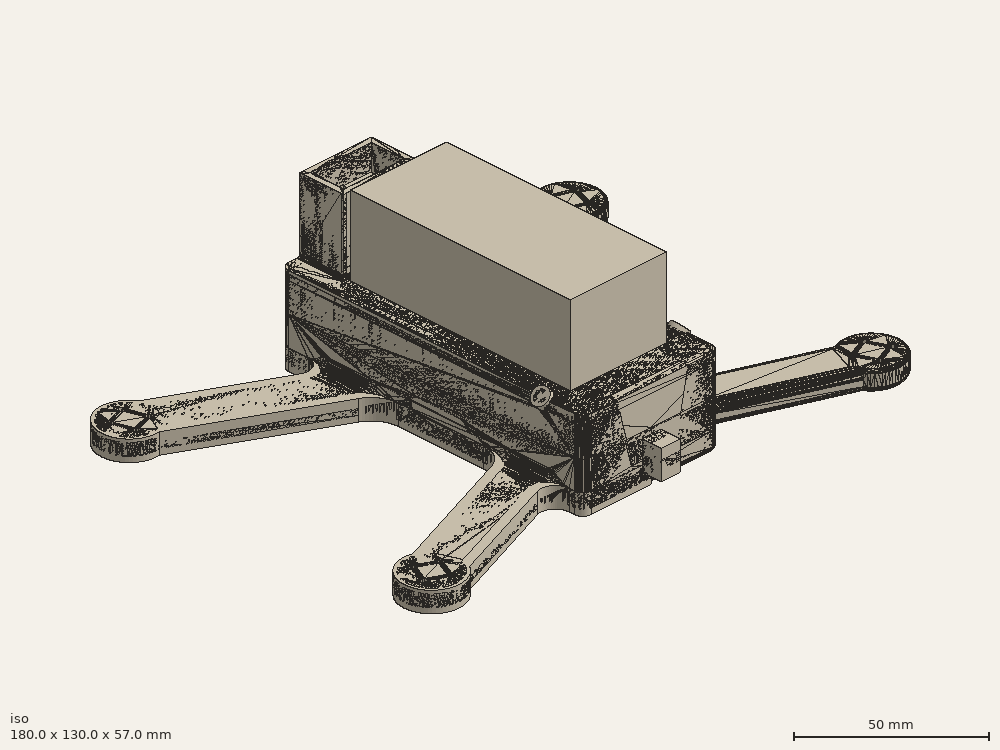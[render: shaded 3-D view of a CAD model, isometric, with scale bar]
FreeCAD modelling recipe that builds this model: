
FCSTD DOCUMENT  (FreeCAD 0.16R6700 (Git))
Label: fuselage3
License: All rights reserved
LicenseURL: http://en.wikipedia.org/wiki/All_rights_reserved
objects: Sketcher::SketchObject×24, PartDesign::Fillet×13, PartDesign::Pocket×12, PartDesign::Pad×11, Part::Fillet×4, Mesh::Feature×3, Part::Mirroring×2, Part::MultiFuse×2, Part::Revolution×1, Part::Cut×1, Part::Cylinder×1
note: 94 computed .brp shape members not serialized (recipe doc carries the construction recipe); baked Part::Feature solids carry a one-line shape summary decoded from their .brp

FEATURE [Mesh::Feature] cam_holder2
FEATURE [Sketcher::SketchObject] Sketch
  sketch-geometry (41):
    g0: LineSegment [constr] StartX=-80 StartY=55 StartZ=0 EndX=-80 EndY=-55 EndZ=0
    g1: LineSegment [constr] StartX=-80 StartY=55 StartZ=0 EndX=-25 EndY=55 EndZ=0
    g2: LineSegment [constr] StartX=-25 StartY=55 StartZ=0 EndX=25 EndY=55 EndZ=0
    g3: LineSegment [constr] StartX=25 StartY=55 StartZ=0 EndX=25 EndY=-55 EndZ=0
    g4: LineSegment [constr] StartX=25 StartY=-55 StartZ=0 EndX=-25 EndY=-55 EndZ=0
    g5: LineSegment [constr] StartX=-80 StartY=-55 StartZ=0 EndX=-25 EndY=-55 EndZ=0
    g6: ArcOfCircle CenterX=-80 CenterY=55 CenterZ=0 NormalX=0 NormalY=0 NormalZ=1 Radius=10 StartAngle=0.531084 EndAngle=4.82619
    g7: LineSegment StartX=-71.3774 StartY=60.0647 StartZ=0 EndX=-32.233 EndY=40.5263 EndZ=0
    g8: LineSegment StartX=-78.8644 StartY=45.0647 StartZ=0 EndX=-30.5341 EndY=20.9413 EndZ=0
    g9: LineSegment StartX=-25 StartY=11.9939 StartZ=0 EndX=-25 EndY=-18.7062 EndZ=0
    g10: ArcOfCircle CenterX=-80 CenterY=-55 CenterZ=0 NormalX=0 NormalY=0 NormalZ=1 Radius=10 StartAngle=1.29221 EndAngle=5.71447
    g11: LineSegment StartX=-77.2501 StartY=-45.3855 StartZ=0 EndX=-31.4609 EndY=-28.059 EndZ=0
    g12: LineSegment StartX=-71.5741 StartY=-60.3855 StartZ=0 EndX=-31.7695 EndY=-45.3236 EndZ=0
    g13: LineSegment StartX=0 StartY=55 StartZ=0 EndX=0 EndY=-55 EndZ=0
    g14: LineSegment [constr] StartX=-77.2501 StartY=-45.3855 StartZ=0 EndX=-71.5741 EndY=-60.3855 EndZ=0
    g15: LineSegment [constr] StartX=-71.3774 StartY=60.0647 StartZ=0 EndX=-78.8644 EndY=45.0647 EndZ=0
    g16: Circle CenterX=-77.5437 CenterY=59.9211 CenterZ=0 NormalX=0 NormalY=0 NormalZ=1 Radius=1.15
    g17: Circle CenterX=-84.9211 CenterY=57.4563 CenterZ=0 NormalX=0 NormalY=0 NormalZ=1 Radius=1.15
    g18: Circle CenterX=-82.4563 CenterY=50.0789 CenterZ=0 NormalX=0 NormalY=0 NormalZ=1 Radius=1.15
    g19: Circle CenterX=-75.0789 CenterY=52.5437 CenterZ=0 NormalX=0 NormalY=0 NormalZ=1 Radius=1.15
    g20: Circle [constr] CenterX=-80 CenterY=55 CenterZ=0 NormalX=0 NormalY=0 NormalZ=1 Radius=5.5
    g21: Circle CenterX=-81.9465 CenterY=-49.856 CenterZ=0 NormalX=0 NormalY=0 NormalZ=1 Radius=1.15
    g22: Circle CenterX=-85.144 CenterY=-56.9465 CenterZ=0 NormalX=0 NormalY=0 NormalZ=1 Radius=1.15
    g23: Circle CenterX=-78.0535 CenterY=-60.144 CenterZ=0 NormalX=0 NormalY=0 NormalZ=1 Radius=1.15
    g24: Circle CenterX=-74.856 CenterY=-53.0535 CenterZ=0 NormalX=0 NormalY=0 NormalZ=1 Radius=1.15
    g25: Circle [constr] CenterX=-80 CenterY=-55 CenterZ=0 NormalX=0 NormalY=0 NormalZ=1 Radius=5.5
    g26: ArcOfCircle CenterX=-35 CenterY=-18.7062 CenterZ=0 NormalX=0 NormalY=0 NormalZ=1 Radius=10 StartAngle=5.07413 EndAngle=6.28319
    g27: ArcOfCircle CenterX=-35 CenterY=11.9939 CenterZ=0 NormalX=0 NormalY=0 NormalZ=1 Radius=10 StartAngle=0 EndAngle=1.10784
    g28: LineSegment StartX=-25 StartY=45 StartZ=0 EndX=-25 EndY=52 EndZ=0
    g29: LineSegment StartX=-22 StartY=55 StartZ=0 EndX=0 EndY=55 EndZ=0
    g30: ArcOfCircle CenterX=-30 CenterY=45 CenterZ=0 NormalX=0 NormalY=0 NormalZ=1 Radius=5 StartAngle=4.24943 EndAngle=6.28319
    g31: LineSegment [constr] StartX=-25 StartY=45 StartZ=0 EndX=-25 EndY=11.9939 EndZ=0
    g32: LineSegment StartX=-25 StartY=-50 StartZ=0 EndX=-25 EndY=-52 EndZ=0
    g33: ArcOfCircle CenterX=-30 CenterY=-50 CenterZ=0 NormalX=0 NormalY=0 NormalZ=1 Radius=5 StartAngle=0 EndAngle=1.93254
    g34: LineSegment StartX=0 StartY=-55 StartZ=0 EndX=-22 EndY=-55 EndZ=0
    g35: ArcOfCircle CenterX=-22 CenterY=52 CenterZ=0 NormalX=0 NormalY=0 NormalZ=1 Radius=3 StartAngle=1.5708 EndAngle=3.14159
    g36: ArcOfCircle CenterX=-22 CenterY=-52 CenterZ=0 NormalX=0 NormalY=0 NormalZ=1 Radius=3 StartAngle=3.14159 EndAngle=4.71239
    g37: LineSegment [constr] StartX=-80 StartY=-55 StartZ=0 EndX=-74.4121 EndY=-52.8855 EndZ=0
    g38: LineSegment [constr] StartX=-80 StartY=-55 StartZ=0 EndX=-78.0535 EndY=-60.144 EndZ=0
    g39: LineSegment [constr] StartX=-77.5437 StartY=59.9211 StartZ=0 EndX=-82.4563 EndY=50.0789 EndZ=0
    g40: LineSegment [constr] StartX=-84.9211 StartY=57.4563 StartZ=0 EndX=-75.0789 EndY=52.5437 EndZ=0
  constraints (110):
    c: Vertical(g0)
    c: Distance(g0) = 110
    c: Coincident(g1,g0)
    c: Horizontal(g1)
    c: Distance(g1) = 55
    c: Coincident(g2,g3)
    c: Coincident(g3,g4)
    c: Horizontal(g2)
    c: Horizontal(g4)
    c: Vertical(g3)
    c: Coincident(g2,g1)
    c: Distance(g2) = 50
    c: Coincident(g5,g0)
    c: Horizontal(g5)
    c: Symmetric(g1,g2,g-2)
    c: Symmetric(g3,g2,g-1)
    c: Coincident(g0,g6)
    c: Radius(g6) = 10
    c: PointOnObject(g13,g-2)
    c: Equal(g6,g10) = 10
    c: Coincident(g7,g0)
    c: Coincident(g0,g10)
    c: Coincident(g6,g7)
    c: Coincident(g6,g8)
    c: Coincident(g10,g11)
    c: Coincident(g10,g12)
    c: DistanceY(g6,g6) = 15
    c: DistanceY(g10,g10) = 15
    c: Coincident(g14,g10)
    c: Coincident(g14,g10)
    c: Coincident(g15,g6)
    c: Coincident(g15,g6)
    c: Coincident(g20,g0)
    c: Radius(g20) = 5.5
    c: Radius(g16) = 1.15
    c: Equal(g16,g17)
    c: Equal(g17,g19)
    c: Equal(g19,g18)
    c: Equal(g20,g25) = 5.5
    c: Equal(g16,g21) = 1.15
    c: Equal(g21,g22)
    c: Equal(g22,g24)
    c: Equal(g24,g23)
    c: Coincident(g25,g0)
    c: Tangent(g11,g26) = -1.5708
    c: Tangent(g9,g26) = 1.5708
    c: Tangent(g9,g27) = 1.5708
    c: Tangent(g8,g27) = 1.5708
    c: Radius(g27) = 10
    c: Vertical(g9)
    c: Radius(g26) = 10
    c: Parallel(g7,g8)
    c: Perpendicular(g7,g15)
    c: PointOnObject(g29,g-2)
    c: Horizontal(g29)
    c: Coincident(g13,g29)
    c: Tangent(g28,g30) = -1.5708
    c: Tangent(g7,g30) = -1.5708
    c: Coincident(g31,g28)
    c: Coincident(g31,g9)
    c: Vertical(g31)
    c: Vertical(g28)
    c: Radius(g30) = 5
    c: Parallel(g11,g12)
    c: Perpendicular(g11,g14)
    c: Coincident(g4,g5)
    c: Vertical(g32)
    c: Tangent(g32,g33) = 1.5708
    c: Tangent(g12,g33) = 1.5708
    c: Radius(g33) = 5
    c: PointOnObject(g32,g31)
    c: Coincident(g34,g13)
    c: Horizontal(g34)
    c: Vertical(g13)
    c: Tangent(g29,g35) = 1.5708
    c: Tangent(g28,g35) = 1.5708
    c: Radius(g35) = 3
    c: PointOnObject(g29,g2)
    c: DistanceY(g28,g29) = 10
    c: PointOnObject(g1,g31)
    c: Tangent(g34,g36) = 1.5708
    c: Tangent(g32,g36) = -1.5708
    c: Radius(g36) = 3
    c: PointOnObject(g34,g4)
    c: PointOnObject(g4,g32)
    c: DistanceY(g4,g32) = 5
    c: Coincident(g37,g0)
    c: PointOnObject(g37,g14)
    c: Perpendicular(g37,g14)
    c: PointOnObject(g24,g37)
    c: PointOnObject(g24,g25)
    c: PointOnObject(g22,g37)
    c: PointOnObject(g22,g25)
    c: Coincident(g38,g0)
    c: PointOnObject(g38,g25)
    c: Parallel(g38,g14)
    c: Coincident(g23,g38)
    c: Symmetric(g21,g23,g37)
    c: PointOnObject(g39,g20)
    c: PointOnObject(g39,g20)
    c: PointOnObject(g40,g20)
    c: PointOnObject(g40,g20)
    c: PointOnObject(g0,g40)
    c: PointOnObject(g0,g39)
    c: Parallel(g39,g15)
    c: Perpendicular(g39,g40)
    c: Coincident(g17,g40)
    c: Coincident(g18,g39)
    c: Coincident(g19,g40)
    c: Coincident(g16,g39)
FEATURE [PartDesign::Pad] Pad
  Length = 7
  Length2 = 100
  Sketch = -> Sketch
  Type = 0
FEATURE [Sketcher::SketchObject] Sketch001
  Placement = pos=(0,0,7) rot=(0,0,1;0rad)
  Support = -> Pad [Face28]
  sketch-geometry (6):
    g0: LineSegment StartX=0 StartY=52 StartZ=0 EndX=-21 EndY=52 EndZ=0
    g1: LineSegment StartX=-22 StartY=51 StartZ=0 EndX=-22 EndY=-51 EndZ=0
    g2: LineSegment StartX=-21 StartY=-52 StartZ=0 EndX=0 EndY=-52 EndZ=0
    g3: LineSegment StartX=0 StartY=-52 StartZ=0 EndX=0 EndY=52 EndZ=0
    g4: ArcOfCircle CenterX=-21 CenterY=-51 CenterZ=0 NormalX=0 NormalY=0 NormalZ=1 Radius=1 StartAngle=3.14159 EndAngle=4.71239
    g5: ArcOfCircle CenterX=-21 CenterY=51 CenterZ=0 NormalX=0 NormalY=0 NormalZ=1 Radius=1 StartAngle=1.5708 EndAngle=3.14159
  constraints (16):
    c: Coincident(g2,g3)
    c: Coincident(g3,g0)
    c: Horizontal(g0)
    c: Horizontal(g2)
    c: Vertical(g1)
    c: Vertical(g3)
    c: PointOnObject(g0,g-2)
    c: Symmetric(g0,g2,g-1)
    c: Tangent(g2,g4) = -1.5708
    c: Tangent(g1,g4) = -1.5708
    c: Radius(g4) = 1
    c: Tangent(g0,g5) = -1.5708
    c: Tangent(g1,g5) = -1.5708
    c: Radius(g5) = 1
    c: DistanceX(g1,g0) = 22
    c: Distance(g3) = 104
FEATURE [PartDesign::Pocket] Pocket
  Length = 2
  Sketch = -> Sketch001
  Type = 0
FEATURE [Sketcher::SketchObject] Sketch002
  Placement = pos=(0,0,7) rot=(0,0,1;0rad)
  Support = -> Pocket [Face5]
  sketch-geometry (12):
    g0: LineSegment StartX=0 StartY=52 StartZ=0 EndX=-21 EndY=52 EndZ=0
    g1: LineSegment StartX=-22 StartY=51 StartZ=0 EndX=-22 EndY=-51 EndZ=0
    g2: LineSegment StartX=-21 StartY=-52 StartZ=0 EndX=0 EndY=-52 EndZ=0
    g3: ArcOfCircle CenterX=-21 CenterY=-51 CenterZ=0 NormalX=0 NormalY=0 NormalZ=1 Radius=1 StartAngle=3.14159 EndAngle=4.71239
    g4: ArcOfCircle CenterX=-21 CenterY=51 CenterZ=0 NormalX=0 NormalY=0 NormalZ=1 Radius=1 StartAngle=1.5708 EndAngle=3.14159
    g5: LineSegment StartX=0 StartY=-52 StartZ=0 EndX=0 EndY=-55 EndZ=0
    g6: LineSegment StartX=0 StartY=-55 StartZ=0 EndX=-22 EndY=-55 EndZ=0
    g7: LineSegment StartX=-25 StartY=-52 StartZ=0 EndX=-25 EndY=52 EndZ=0
    g8: LineSegment StartX=-22 StartY=55 StartZ=0 EndX=0 EndY=55 EndZ=0
    g9: LineSegment StartX=0 StartY=55 StartZ=0 EndX=0 EndY=52 EndZ=0
    g10: ArcOfCircle CenterX=-22 CenterY=-52 CenterZ=0 NormalX=0 NormalY=0 NormalZ=1 Radius=3 StartAngle=3.14159 EndAngle=4.71239
    g11: ArcOfCircle CenterX=-22 CenterY=52 CenterZ=0 NormalX=0 NormalY=0 NormalZ=1 Radius=3 StartAngle=1.5708 EndAngle=3.14159
  constraints (31):
    c: Horizontal(g0)
    c: Horizontal(g2)
    c: Vertical(g1)
    c: PointOnObject(g0,g-2)
    c: Symmetric(g0,g2,g-1)
    c: Tangent(g2,g3) = -1.5708
    c: Tangent(g1,g3) = -1.5708
    c: Radius(g3) = 1
    c: Tangent(g0,g4) = -1.5708
    c: Tangent(g1,g4) = -1.5708
    c: Radius(g4) = 1
    c: DistanceX(g1,g0) = 22
    c: Coincident(g5,g2)
    c: Vertical(g5)
    c: Coincident(g5,g6)
    c: Horizontal(g6)
    c: Vertical(g7)
    c: Horizontal(g8)
    c: Coincident(g8,g9)
    c: Coincident(g9,g0)
    c: Vertical(g9)
    c: Tangent(g6,g10) = 1.5708
    c: Tangent(g7,g10) = 1.5708
    c: Radius(g10) = 3
    c: Tangent(g8,g11) = 1.5708
    c: Tangent(g7,g11) = 1.5708
    c: Radius(g11) = 3
    c: DistanceY(g5,g8) = 110
    c: DistanceX(g7,g1) = 3
    c: DistanceY(g0,g8) = 3
    c: DistanceY(g6,g2) = 3
FEATURE [PartDesign::Pad] Pad001  label="height here"
  Length = 10
  Length2 = 100
  Sketch = -> Sketch002
  Type = 0
FEATURE [Part::Fillet] Fillet
  Base = -> Pad001
  Edges = 9 edges r=3: [Edge10,Edge34,Edge35,Edge42,Edge45,Edge48,Edge56,Edge57,Edge86]
FEATURE [Part::Fillet] Fillet001
  Base = -> Fillet
  Edges = 17 edges r=2: [Edge3,Edge6,Edge14,Edge15,Edge16,Edge17,Edge18,Edge19,Edge20,Edge21,Edge22,Edge23,Edge24,Edge26,Edge27,Edge28,Edge29]
FEATURE [Part::Fillet] Fillet002  label="body half"
  Base = -> Fillet001
  Edges = 2 edges r=1: [Edge10,Edge159]
FEATURE [Sketcher::SketchObject] Sketch003
  ExternalGeometry = -> [Fillet002]
  Placement = pos=(0,0,0) rot=(1,0,0;3.14159rad)
  Support = -> Fillet002 [Face14]
  sketch-geometry (8):
    g0: Circle CenterX=-78.0535 CenterY=60.144 CenterZ=0 NormalX=0 NormalY=0 NormalZ=1 Radius=2.5
    g1: Circle CenterX=-85.144 CenterY=56.9465 CenterZ=0 NormalX=0 NormalY=0 NormalZ=1 Radius=2.5
    g2: Circle CenterX=-74.856 CenterY=53.0535 CenterZ=0 NormalX=0 NormalY=0 NormalZ=1 Radius=2.5
    g3: Circle CenterX=-81.9465 CenterY=49.856 CenterZ=0 NormalX=0 NormalY=0 NormalZ=1 Radius=2.5
    g4: Circle CenterX=-75.0789 CenterY=-52.5437 CenterZ=0 NormalX=0 NormalY=0 NormalZ=1 Radius=2.5
    g5: Circle CenterX=-82.4563 CenterY=-50.0789 CenterZ=0 NormalX=0 NormalY=0 NormalZ=1 Radius=2.5
    g6: Circle CenterX=-84.9211 CenterY=-57.4563 CenterZ=0 NormalX=0 NormalY=0 NormalZ=1 Radius=2.5
    g7: Circle CenterX=-77.5437 CenterY=-59.9211 CenterZ=0 NormalX=0 NormalY=0 NormalZ=1 Radius=2.5
  constraints (16):
    c: Coincident(g0,g-5)
    c: Radius(g0) = 2.5
    c: Equal(g0,g1) = 2.5
    c: Coincident(g1,g-4)
    c: Coincident(g2,g-6)
    c: Equal(g0,g3) = 2.5
    c: Coincident(g3,g-3)
    c: Equal(g2,g0)
    c: Coincident(g4,g-7)
    c: Coincident(g5,g-8)
    c: Coincident(g6,g-9)
    c: Coincident(g7,g-10)
    c: Equal(g6,g7)
    c: Equal(g7,g5)
    c: Equal(g5,g4)
    c: Equal(g4,g0)
FEATURE [PartDesign::Pocket] Pocket001
  Length = 5
  Sketch = -> Sketch003
  Type = 0
FEATURE [Part::Mirroring] Part__Mirroring  label="Pocket001 (Mirror #1)"
  Base = (0,0,0)
  Normal = (1,0,0)
  Source = -> Pocket001
FEATURE [Part::MultiFuse] Fusion  label="body"
  Shapes = -> [Part__Mirroring,Pocket001]
FEATURE [Sketcher::SketchObject] Sketch009
  Placement = pos=(-15,43,6) rot=(-1,0,0;1.5708rad)
  sketch-geometry (8):
    g0: LineSegment StartX=0 StartY=0 StartZ=0 EndX=20 EndY=0 EndZ=0
    g1: LineSegment StartX=20 StartY=0 StartZ=0 EndX=20 EndY=-26 EndZ=0
    g2: LineSegment StartX=10 StartY=-26 StartZ=0 EndX=0 EndY=-26 EndZ=0
    g3: LineSegment StartX=0 StartY=-26 StartZ=0 EndX=0 EndY=0 EndZ=0
    g4: LineSegment StartX=20 StartY=-26 StartZ=0 EndX=20 EndY=-41 EndZ=0
    g5: LineSegment StartX=20 StartY=-41 StartZ=0 EndX=10 EndY=-41 EndZ=0
    g6: LineSegment StartX=10 StartY=-41 StartZ=0 EndX=10 EndY=-26 EndZ=0
    g7: LineSegment [constr] StartX=10 StartY=-26 StartZ=0 EndX=20 EndY=-26 EndZ=0
  constraints (22):
    c: Coincident(g0,g1)
    c: Coincident(g2,g3)
    c: Coincident(g3,g0)
    c: Horizontal(g0)
    c: Horizontal(g2)
    c: Vertical(g1)
    c: Vertical(g3)
    c: Distance(g0) = 20
    c: DistanceY(g1,g1) = 26
    c: Coincident(g4,g1)
    c: Vertical(g4)
    c: DistanceY(g4,g4) = 15
    c: Coincident(g5,g4)
    c: Horizontal(g5)
    c: Distance(g5) = 10
    c: Coincident(g6,g5)
    c: Vertical(g6)
    c: Coincident(g2,g6)
    c: Coincident(g7,g2)
    c: Coincident(g7,g1)
    c: Horizontal(g7)
    c: Coincident(g0,g-1)
FEATURE [PartDesign::Pad] Pad003  label="video_tx_base"
  Length = 6
  Length2 = 100
  Placement = pos=(-15,43,6) rot=(-1,0,0;1.5708rad)
  Sketch = -> Sketch009
  Type = 0
FEATURE [Sketcher::SketchObject] Sketch010
  ExternalGeometry = -> [Pad003]
  Placement = pos=(-15,49,6) rot=(-1,0,0;1.5708rad)
  Support = -> Pad003 [Face9]
  sketch-geometry (8):
    g0: LineSegment StartX=0.5 StartY=-3 StartZ=0 EndX=19.5 EndY=-3 EndZ=0
    g1: LineSegment StartX=19.5 StartY=-3 StartZ=0 EndX=19.5 EndY=-23 EndZ=0
    g2: LineSegment StartX=19.5 StartY=-23 StartZ=0 EndX=0.5 EndY=-23 EndZ=0
    g3: LineSegment StartX=0.5 StartY=-23 StartZ=0 EndX=0.5 EndY=-3 EndZ=0
    g4: LineSegment StartX=10 StartY=-26 StartZ=0 EndX=20 EndY=-26 EndZ=0
    g5: LineSegment StartX=20 StartY=-26 StartZ=0 EndX=20 EndY=-41 EndZ=0
    g6: LineSegment StartX=20 StartY=-41 StartZ=0 EndX=10 EndY=-41 EndZ=0
    g7: LineSegment StartX=10 StartY=-26 StartZ=0 EndX=10 EndY=-41 EndZ=0
  constraints (21):
    c: Coincident(g0,g1)
    c: Coincident(g1,g2)
    c: Coincident(g2,g3)
    c: Coincident(g3,g0)
    c: Horizontal(g0)
    c: Horizontal(g2)
    c: Vertical(g1)
    c: Vertical(g3)
    c: Coincident(g4,g5)
    c: Coincident(g5,g6)
    c: Horizontal(g4)
    c: Horizontal(g6)
    c: Vertical(g5)
    c: Coincident(g4,g-3)
    c: Coincident(g5,g-4)
    c: Distance(g2) = 19
    c: Distance(g1) = 20
    c: DistanceX(g-1,g0) = 0.5
    c: DistanceY(g0,g-1) = 3
    c: Coincident(g7,g4)
    c: Coincident(g7,g6)
FEATURE [PartDesign::Pad] Pad004  label="video_tx"
  Length = 3
  Length2 = 100
  Placement = pos=(-15,43,6) rot=(-1,0,0;1.5708rad)
  Sketch = -> Sketch010
  Type = 0
FEATURE [Part::Fillet] Fillet003
  Base = -> Fusion
  Edges = 10 edges r=1: [Edge272,Edge274,Edge276,Edge278,Edge279,Edge367,Edge369,Edge371,Edge372,Edge373]
FEATURE [Sketcher::SketchObject] Sketch011
  Placement = pos=(0,0,17) rot=(0,0,1;0rad)
  Support = -> Fillet003 [Face2]
  sketch-geometry (16):
    g0: LineSegment StartX=-22 StartY=55 StartZ=0 EndX=22 EndY=55 EndZ=0
    g1: LineSegment StartX=25 StartY=52 StartZ=0 EndX=25 EndY=-52 EndZ=0
    g2: LineSegment StartX=22 StartY=-55 StartZ=0 EndX=-22 EndY=-55 EndZ=0
    g3: LineSegment StartX=-25 StartY=-52 StartZ=0 EndX=-25 EndY=52 EndZ=0
    g4: LineSegment StartX=-22 StartY=53.5 StartZ=0 EndX=22 EndY=53.5 EndZ=0
    g5: LineSegment StartX=23.5 StartY=52 StartZ=0 EndX=23.5 EndY=-52 EndZ=0
    g6: LineSegment StartX=22 StartY=-53.5 StartZ=0 EndX=-22 EndY=-53.5 EndZ=0
    g7: LineSegment StartX=-23.5 StartY=-52 StartZ=0 EndX=-23.5 EndY=52 EndZ=0
    g8: ArcOfCircle CenterX=-22 CenterY=-52 CenterZ=0 NormalX=0 NormalY=0 NormalZ=1 Radius=1.5 StartAngle=3.14159 EndAngle=4.71239
    g9: ArcOfCircle CenterX=-22 CenterY=52 CenterZ=0 NormalX=0 NormalY=0 NormalZ=1 Radius=1.5 StartAngle=1.5708 EndAngle=3.14159
    g10: ArcOfCircle CenterX=22 CenterY=52 CenterZ=0 NormalX=0 NormalY=0 NormalZ=1 Radius=1.5 StartAngle=0 EndAngle=1.5708
    g11: ArcOfCircle CenterX=22 CenterY=-52 CenterZ=0 NormalX=0 NormalY=0 NormalZ=1 Radius=1.5 StartAngle=4.71239 EndAngle=6.28319
    g12: ArcOfCircle CenterX=22 CenterY=-52 CenterZ=0 NormalX=0 NormalY=0 NormalZ=1 Radius=3 StartAngle=4.71239 EndAngle=6.28319
    g13: ArcOfCircle CenterX=-22 CenterY=-52 CenterZ=0 NormalX=0 NormalY=0 NormalZ=1 Radius=3 StartAngle=3.14159 EndAngle=4.71239
    g14: ArcOfCircle CenterX=-22 CenterY=52 CenterZ=0 NormalX=0 NormalY=0 NormalZ=1 Radius=3 StartAngle=1.5708 EndAngle=3.14159
    g15: ArcOfCircle CenterX=22 CenterY=52 CenterZ=0 NormalX=0 NormalY=0 NormalZ=1 Radius=3 StartAngle=0 EndAngle=1.5708
  constraints (39):
    c: Horizontal(g0)
    c: Horizontal(g2)
    c: Vertical(g1)
    c: Vertical(g3)
    c: Horizontal(g4)
    c: Horizontal(g6)
    c: Vertical(g5)
    c: Vertical(g7)
    c: Tangent(g6,g8) = 1.5708
    c: Tangent(g7,g8) = 1.5708
    c: Tangent(g7,g9) = 1.5708
    c: Tangent(g4,g9) = 1.5708
    c: Tangent(g4,g10) = 1.5708
    c: Tangent(g5,g10) = 1.5708
    c: Tangent(g5,g11) = 1.5708
    c: Tangent(g6,g11) = 1.5708
    c: Tangent(g1,g12) = 1.5708
    c: Tangent(g2,g12) = 1.5708
    c: Tangent(g2,g13) = 1.5708
    c: Tangent(g3,g13) = 1.5708
    c: Tangent(g3,g14) = 1.5708
    c: Tangent(g0,g14) = 1.5708
    c: Tangent(g0,g15) = 1.5708
    c: Tangent(g1,g15) = 1.5708
    c: Radius(g15) = 3
    c: Equal(g15,g14)
    c: Equal(g15,g13)
    c: Equal(g15,g12)
    c: Radius(g8) = 1.5
    c: Equal(g8,g11)
    c: Equal(g8,g10)
    c: Equal(g8,g9)
    c: DistanceY(g2,g0) = 110
    c: DistanceX(g3,g1) = 50
    c: Symmetric(g0,g0,g-2)
    c: Symmetric(g3,g3,g-1)
    c: Symmetric(g7,g7,g-1)
    c: Symmetric(g4,g4,g-2)
    c: Coincident(g8,g13)
FEATURE [PartDesign::Pad] Pad005
  Length = 10
  Length2 = 100
  Sketch = -> Sketch011
  Type = 0
FEATURE [PartDesign::Fillet] Fillet004
  Base = -> Pad005 [Edge489,Edge542,Edge491,Edge497,Edge493,Edge495,Edge479,Edge481,Edge487,Edge483,Edge485]
  Radius = 1
FEATURE [Mesh::Feature] cc3d_model  label="cc3d-model"
  Placement = pos=(0,0,15) rot=(0,0,-1;1.5708rad)
FEATURE [Sketcher::SketchObject] Sketch012
  Placement = pos=(25,0,0) rot=(0.57735,0.57735,0.57735;2.0944rad)
  Support = -> Fillet004 [Face67]
  sketch-geometry (4):
    g0: ArcOfCircle CenterX=-5 CenterY=13 CenterZ=0 NormalX=0 NormalY=0 NormalZ=1 Radius=5 StartAngle=1.5708 EndAngle=4.71239
    g1: ArcOfCircle CenterX=5 CenterY=13 CenterZ=0 NormalX=0 NormalY=0 NormalZ=1 Radius=5 StartAngle=4.71239 EndAngle=7.85398
    g2: LineSegment StartX=-5 StartY=8 StartZ=0 EndX=5 EndY=8 EndZ=0
    g3: LineSegment StartX=-5 StartY=18 StartZ=0 EndX=5 EndY=18 EndZ=0
  constraints (10):
    c: Tangent(g0,g3) = 1.5708
    c: Tangent(g0,g2) = -1.5708
    c: Tangent(g2,g1) = -1.5708
    c: Tangent(g3,g1) = 1.5708
    c: Horizontal(g2)
    c: Equal(g0,g1)
    c: DistanceY(g0,g0) = 10
    c: Distance(g3) = 10
    c: DistanceY(g-1,g1) = 13
    c: DistanceX(g0,g-1) = 5
FEATURE [PartDesign::Pocket] Pocket002
  Length = 5
  Sketch = -> Sketch012
  Type = 0
FEATURE [Sketcher::SketchObject] Sketch013
  Placement = pos=(0,0,5) rot=(0,0,1;0rad)
  Support = -> Pocket002 [Face14]
  sketch-geometry (8):
    g0: Circle CenterX=-15.25 CenterY=15.25 CenterZ=0 NormalX=0 NormalY=0 NormalZ=1 Radius=1.7
    g1: LineSegment [constr] StartX=-15.25 StartY=15.25 StartZ=0 EndX=15.25 EndY=15.25 EndZ=0
    g2: LineSegment [constr] StartX=15.25 StartY=15.25 StartZ=0 EndX=15.25 EndY=-15.25 EndZ=0
    g3: LineSegment [constr] StartX=15.25 StartY=-15.25 StartZ=0 EndX=-15.25 EndY=-15.25 EndZ=0
    g4: LineSegment [constr] StartX=-15.25 StartY=-15.25 StartZ=0 EndX=-15.25 EndY=15.25 EndZ=0
    g5: Circle CenterX=15.25 CenterY=15.25 CenterZ=0 NormalX=0 NormalY=0 NormalZ=1 Radius=1.7
    g6: Circle CenterX=15.25 CenterY=-15.25 CenterZ=0 NormalX=0 NormalY=0 NormalZ=1 Radius=1.7
    g7: Circle CenterX=-15.25 CenterY=-15.25 CenterZ=0 NormalX=0 NormalY=0 NormalZ=1 Radius=1.7
  constraints (22):
    c: Radius(g0) = 1.7
    c: Coincident(g1,g2)
    c: Coincident(g2,g3)
    c: Coincident(g3,g4)
    c: Coincident(g4,g1)
    c: Horizontal(g1)
    c: Horizontal(g3)
    c: Vertical(g2)
    c: Vertical(g4)
    c: Coincident(g1,g0)
    c: Distance(g1) = 30.5
    c: Distance(g4) = 30.5
    c: Symmetric(g3,g2,g-2)
    c: Symmetric(g1,g2,g-1)
    c: Equal(g0,g5) = 1.7
    c: Coincident(g1,g1)
    c: Coincident(g6,g2)
    c: Equal(g0,g7) = 1.7
    c: Coincident(g1,g3)
    c: Equal(g7,g6)
    c: Coincident(g3,g7)
    c: Coincident(g1,g5)
FEATURE [PartDesign::Pocket] Pocket003
  Length = 5
  Sketch = -> Sketch013
  Type = 0
FEATURE [Sketcher::SketchObject] Sketch014
  ExternalGeometry = -> [Pocket003]
  Placement = pos=(0,0,0) rot=(1,0,0;3.14159rad)
  Support = -> Pocket003 [Face37]
  sketch-geometry (4):
    g0: Circle CenterX=-15.25 CenterY=15.25 CenterZ=0 NormalX=0 NormalY=0 NormalZ=1 Radius=5
    g1: Circle CenterX=15.25 CenterY=15.25 CenterZ=0 NormalX=0 NormalY=0 NormalZ=1 Radius=5
    g2: Circle CenterX=15.25 CenterY=-15.25 CenterZ=0 NormalX=0 NormalY=0 NormalZ=1 Radius=5
    g3: Circle CenterX=-15.25 CenterY=-15.25 CenterZ=0 NormalX=0 NormalY=0 NormalZ=1 Radius=5
  constraints (8):
    c: Coincident(g0,g-3)
    c: Radius(g0) = 5
    c: Equal(g0,g1) = 5
    c: Coincident(g1,g-4)
    c: Coincident(g2,g-5)
    c: Coincident(g3,g-6)
    c: Equal(g0,g3)
    c: Equal(g3,g2)
FEATURE [PartDesign::Pocket] Pocket004
  Length = 2
  Sketch = -> Sketch014
  Type = 0
FEATURE [PartDesign::Fillet] Fillet005
  Base = -> Pocket004 [Edge172,Edge155,Edge157,Edge170]
  Radius = 1
FEATURE [Sketcher::SketchObject] Sketch015
  Placement = pos=(0,0,27) rot=(0,0,1;0rad)
  Support = -> Fillet005 [Face223]
  sketch-geometry (8):
    g0: LineSegment StartX=-22 StartY=55 StartZ=0 EndX=22 EndY=55 EndZ=0
    g1: LineSegment StartX=25 StartY=52 StartZ=0 EndX=25 EndY=-52 EndZ=0
    g2: LineSegment StartX=22 StartY=-55 StartZ=0 EndX=-22 EndY=-55 EndZ=0
    g3: LineSegment StartX=-25 StartY=-52 StartZ=0 EndX=-25 EndY=52 EndZ=0
    g4: ArcOfCircle CenterX=-22 CenterY=52 CenterZ=0 NormalX=0 NormalY=0 NormalZ=1 Radius=3 StartAngle=1.5708 EndAngle=3.14159
    g5: ArcOfCircle CenterX=22 CenterY=52 CenterZ=0 NormalX=0 NormalY=0 NormalZ=1 Radius=3 StartAngle=0 EndAngle=1.5708
    g6: ArcOfCircle CenterX=22 CenterY=-52 CenterZ=0 NormalX=0 NormalY=0 NormalZ=1 Radius=3 StartAngle=4.71239 EndAngle=6.28319
    g7: ArcOfCircle CenterX=-22 CenterY=-52 CenterZ=0 NormalX=0 NormalY=0 NormalZ=1 Radius=3 StartAngle=3.14159 EndAngle=4.71239
  constraints (19):
    c: Horizontal(g2)
    c: Vertical(g1)
    c: Vertical(g3)
    c: Tangent(g0,g4) = 1.5708
    c: Tangent(g3,g4) = 1.5708
    c: Tangent(g0,g5) = 1.5708
    c: Tangent(g1,g5) = 1.5708
    c: Tangent(g1,g6) = 1.5708
    c: Tangent(g2,g6) = 1.5708
    c: Tangent(g2,g7) = 1.5708
    c: Tangent(g3,g7) = 1.5708
    c: Radius(g7) = 3
    c: Equal(g7,g6)
    c: Equal(g7,g5)
    c: Equal(g7,g4)
    c: Distance(g0,g2) = 110
    c: Symmetric(g0,g2,g-1)
    c: Symmetric(g0,g0,g-2)
    c: DistanceX(g3,g1) = 50
FEATURE [PartDesign::Pad] Pad006
  Length = 3
  Length2 = 100
  Sketch = -> Sketch015
  Type = 0
FEATURE [Sketcher::SketchObject] Sketch016
  Placement = pos=(0,0,30) rot=(0,0,1;0rad)
  Support = -> Pad006 [Face1]
  sketch-geometry (8):
    g0: LineSegment StartX=-16 StartY=53 StartZ=0 EndX=6 EndY=53 EndZ=0
    g1: LineSegment StartX=6 StartY=53 StartZ=0 EndX=6 EndY=41 EndZ=0
    g2: LineSegment StartX=6 StartY=41 StartZ=0 EndX=-16 EndY=41 EndZ=0
    g3: LineSegment StartX=-16 StartY=41 StartZ=0 EndX=-16 EndY=53 EndZ=0
    g4: LineSegment StartX=-18 StartY=55 StartZ=0 EndX=8 EndY=55 EndZ=0
    g5: LineSegment StartX=8 StartY=55 StartZ=0 EndX=8 EndY=39 EndZ=0
    g6: LineSegment StartX=8 StartY=39 StartZ=0 EndX=-18 EndY=39 EndZ=0
    g7: LineSegment StartX=-18 StartY=39 StartZ=0 EndX=-18 EndY=55 EndZ=0
  constraints (24):
    c: Coincident(g0,g1)
    c: Coincident(g1,g2)
    c: Coincident(g2,g3)
    c: Coincident(g3,g0)
    c: Horizontal(g0)
    c: Horizontal(g2)
    c: Vertical(g1)
    c: Vertical(g3)
    c: DistanceY(g1,g1) = 12
    c: Distance(g0) = 22
    c: DistanceX(g-1,g1) = 6
    c: DistanceY(g-1,g1) = 41
    c: Coincident(g4,g5)
    c: Coincident(g5,g6)
    c: Coincident(g6,g7)
    c: Coincident(g7,g4)
    c: Horizontal(g4)
    c: Horizontal(g6)
    c: Vertical(g5)
    c: Vertical(g7)
    c: DistanceY(g0,g4) = 2
    c: DistanceX(g4,g0) = 2
    c: DistanceX(g0,g4) = 2
    c: DistanceY(g5,g1) = 2
FEATURE [PartDesign::Pad] Pad007
  Length = 25
  Length2 = 100
  Sketch = -> Sketch016
  Type = 0
FEATURE [Sketcher::SketchObject] Sketch017
  ExternalGeometry = -> [Pad007]
  Placement = pos=(0,0,30) rot=(0,0,1;0rad)
  Support = -> Pad007 [Face97]
  sketch-geometry (4):
    g0: LineSegment StartX=-16 StartY=53 StartZ=0 EndX=6 EndY=53 EndZ=0
    g1: LineSegment StartX=6 StartY=53 StartZ=0 EndX=6 EndY=41 EndZ=0
    g2: LineSegment StartX=6 StartY=41 StartZ=0 EndX=-16 EndY=41 EndZ=0
    g3: LineSegment StartX=-16 StartY=41 StartZ=0 EndX=-16 EndY=53 EndZ=0
  constraints (10):
    c: Coincident(g0,g1)
    c: Coincident(g1,g2)
    c: Coincident(g2,g3)
    c: Coincident(g3,g0)
    c: Horizontal(g0)
    c: Horizontal(g2)
    c: Vertical(g1)
    c: Vertical(g3)
    c: Coincident(g1,g-4)
    c: Coincident(g0,g-3)
FEATURE [PartDesign::Pocket] Pocket005
  Length = 5
  Sketch = -> Sketch017
  Type = 0
FEATURE [PartDesign::Fillet] Fillet006
  Base = -> Pocket005 [Edge13,Edge14,Edge15]
  Radius = 1
FEATURE [Sketcher::SketchObject] Sketch018
  Placement = pos=(-17.5,-43,30) rot=(0,0,1;0rad)
  sketch-geometry (4):
    g0: LineSegment StartX=0 StartY=80 StartZ=0 EndX=35 EndY=80 EndZ=0
    g1: LineSegment StartX=35 StartY=80 StartZ=0 EndX=35 EndY=0 EndZ=0
    g2: LineSegment StartX=35 StartY=0 StartZ=0 EndX=0 EndY=0 EndZ=0
    g3: LineSegment StartX=0 StartY=0 StartZ=0 EndX=0 EndY=80 EndZ=0
  constraints (11):
    c: Coincident(g0,g1)
    c: Coincident(g1,g2)
    c: Coincident(g2,g3)
    c: Coincident(g3,g0)
    c: Horizontal(g0)
    c: Horizontal(g2)
    c: Vertical(g1)
    c: Vertical(g3)
    c: Coincident(g2,g-1)
    c: Distance(g3) = 80
    c: Distance(g2) = 35
FEATURE [PartDesign::Pad] Pad008  label="battery"
  Length = 27
  Length2 = 100
  Placement = pos=(-17.5,-43,30) rot=(0,0,1;0rad)
  Sketch = -> Sketch018
  Type = 0
FEATURE [Sketcher::SketchObject] Sketch019
  Placement = pos=(0,0,30) rot=(0,0,1;0rad)
  Support = -> Fillet006 [Face1]
  sketch-geometry (13):
    g0: ArcOfCircle CenterX=20 CenterY=-30 CenterZ=0 NormalX=0 NormalY=0 NormalZ=1 Radius=2.5 StartAngle=3.14159 EndAngle=6.28319
    g1: ArcOfCircle CenterX=20 CenterY=-25 CenterZ=0 NormalX=0 NormalY=0 NormalZ=1 Radius=2.5 StartAngle=0 EndAngle=3.14159
    g2: LineSegment StartX=22.5 StartY=-30 StartZ=0 EndX=22.5 EndY=-25 EndZ=0
    g3: LineSegment StartX=17.5 StartY=-30 StartZ=0 EndX=17.5 EndY=-25 EndZ=0
    g4: LineSegment [constr] StartX=20 StartY=-32.5 StartZ=0 EndX=20 EndY=-22.5 EndZ=0
    g5: ArcOfCircle CenterX=-20 CenterY=10 CenterZ=0 NormalX=0 NormalY=0 NormalZ=1 Radius=1 StartAngle=0 EndAngle=3.14159
    g6: ArcOfCircle CenterX=-20 CenterY=-10 CenterZ=0 NormalX=0 NormalY=0 NormalZ=1 Radius=1 StartAngle=3.14159 EndAngle=6.28319
    g7: LineSegment StartX=-21 StartY=10 StartZ=0 EndX=-21 EndY=-10 EndZ=0
    g8: LineSegment StartX=-19 StartY=10 StartZ=0 EndX=-19 EndY=-10 EndZ=0
    g9: ArcOfCircle CenterX=20 CenterY=10 CenterZ=0 NormalX=0 NormalY=0 NormalZ=1 Radius=1 StartAngle=0 EndAngle=3.14159
    g10: ArcOfCircle CenterX=20 CenterY=-10 CenterZ=0 NormalX=0 NormalY=0 NormalZ=1 Radius=1 StartAngle=3.14159 EndAngle=6.28319
    g11: LineSegment StartX=19 StartY=10 StartZ=0 EndX=19 EndY=-10 EndZ=0
    g12: LineSegment StartX=21 StartY=10 StartZ=0 EndX=21 EndY=-10 EndZ=0
  constraints (34):
    c: Tangent(g0,g3) = 1.5708
    c: Tangent(g0,g2) = -1.5708
    c: Tangent(g2,g1) = -1.5708
    c: Tangent(g3,g1) = 1.5708
    c: Equal(g0,g1)
    c: PointOnObject(g4,g0)
    c: PointOnObject(g4,g1)
    c: PointOnObject(g1,g4)
    c: Distance(g4) = 10
    c: Tangent(g5,g8) = 1.5708
    c: Tangent(g5,g7) = -1.5708
    c: Tangent(g7,g6) = -1.5708
    c: Tangent(g8,g6) = 1.5708
    c: Vertical(g7)
    c: Equal(g5,g6)
    c: DistanceY(g6,g5) = 20
    c: Tangent(g9,g12) = 1.5708
    c: Tangent(g9,g11) = -1.5708
    c: Tangent(g11,g10) = -1.5708
    c: Tangent(g12,g10) = 1.5708
    c: Vertical(g11)
    c: Equal(g9,g10)
    c: DistanceY(g10,g9) = 20
    c: Radius(g9) = 1
    c: Radius(g5) = 1
    c: Symmetric(g5,g6,g-1)
    c: Symmetric(g9,g10,g-1)
    c: Symmetric(g10,g6,g-2)
    c: DistanceX(g6,g9) = 40
    c: PointOnObject(g0,g4)
    c: Radius(g0) = 2.5
    c: Vertical(g4)
    c: DistanceX(g-1,g0) = 20
    c: DistanceY(g1,g-1) = 25
FEATURE [PartDesign::Pocket] Pocket006
  Length = 5
  Sketch = -> Sketch019
  Type = 0
FEATURE [Mesh::Feature] cam_holder2001  label="cam+holder2"
  Placement = pos=(-6.5,-51,13) rot=(1,0,0;1.22173rad)
FEATURE [Sketcher::SketchObject] Sketch020
  Placement = pos=(0,-55,0) rot=(1,0,0;1.5708rad)
  Support = -> Pocket006 [Face44]
  sketch-geometry (4):
    g0: LineSegment StartX=-3.5 StartY=15 StartZ=0 EndX=3.5 EndY=15 EndZ=0
    g1: LineSegment StartX=3.5 StartY=15 StartZ=0 EndX=3.5 EndY=5 EndZ=0
    g2: LineSegment StartX=3.5 StartY=5 StartZ=0 EndX=-3.5 EndY=5 EndZ=0
    g3: LineSegment StartX=-3.5 StartY=5 StartZ=0 EndX=-3.5 EndY=15 EndZ=0
  constraints (12):
    c: Coincident(g0,g1)
    c: Coincident(g1,g2)
    c: Coincident(g2,g3)
    c: Coincident(g3,g0)
    c: Horizontal(g0)
    c: Horizontal(g2)
    c: Vertical(g1)
    c: Vertical(g3)
    c: DistanceX(g2,g2) = 7
    c: DistanceY(g3,g3) = 10
    c: Symmetric(g1,g2,g-2)
    c: DistanceY(g-1,g1) = 5
FEATURE [PartDesign::Pad] Pad009
  Length = 7
  Length2 = 100
  Sketch = -> Sketch020
  Type = 0
FEATURE [Sketcher::SketchObject] Sketch021
  Placement = pos=(-3.5,0,0) rot=(0.57735,-0.57735,-0.57735;2.0944rad)
  Support = -> Pad009 [Face84]
  sketch-geometry (1):
    g0: Circle CenterX=58 CenterY=12 CenterZ=0 NormalX=0 NormalY=0 NormalZ=1 Radius=1.7
  constraints (3):
    c: Radius(g0) = 1.7
    c: DistanceY(g-1,g0) = 12
    c: DistanceX(g-1,g0) = 58
FEATURE [PartDesign::Pocket] Pocket007
  Length = 10
  Sketch = -> Sketch021
  Type = 0
FEATURE [Sketcher::SketchObject] Sketch022
  Placement = pos=(0,-55,0) rot=(1,0,0;1.5708rad)
  Support = -> Pocket007 [Face45]
  sketch-geometry (9):
    g0: LineSegment StartX=9 StartY=9 StartZ=0 EndX=15 EndY=39 EndZ=0
    g1: LineSegment StartX=15 StartY=39 StartZ=0 EndX=-15 EndY=39 EndZ=0
    g2: LineSegment StartX=-15 StartY=39 StartZ=0 EndX=-7 EndY=9 EndZ=0
    g3: LineSegment StartX=3.5 StartY=9 StartZ=0 EndX=3.5 EndY=15 EndZ=0
    g4: LineSegment StartX=3.5 StartY=15 StartZ=0 EndX=-3.5 EndY=15 EndZ=0
    g5: LineSegment StartX=-3.5 StartY=15 StartZ=0 EndX=-3.5 EndY=9 EndZ=0
    g6: LineSegment StartX=3.5 StartY=9 StartZ=0 EndX=9 EndY=9 EndZ=0
    g7: LineSegment StartX=-7 StartY=9 StartZ=0 EndX=-3.5 EndY=9 EndZ=0
    g8: LineSegment [constr] StartX=-3.5 StartY=9 StartZ=0 EndX=3.5 EndY=9 EndZ=0
  constraints (27):
    c: Coincident(g6,g0)
    c: Coincident(g0,g1)
    c: Coincident(g1,g2)
    c: Horizontal(g1)
    c: Symmetric(g0,g1,g-2)
    c: Distance(g1) = 30
    c: DistanceY(g6,g0) = 30
    c: DistanceY(g-1,g6) = 9
    c: DistanceX(g2,g-1) = 7
    c: Coincident(g3,g4)
    c: Coincident(g4,g5)
    c: Horizontal(g4)
    c: Vertical(g3)
    c: Vertical(g5)
    c: Distance(g4) = 7
    c: Symmetric(g3,g4,g-2)
    c: PointOnObject(g6,g3)
    c: Coincident(g7,g2)
    c: Coincident(g7,g5)
    c: Horizontal(g7)
    c: Coincident(g8,g5)
    c: Coincident(g8,g3)
    c: Horizontal(g8)
    c: DistanceY(g3,g3) = 6
    c: Coincident(g3,g6)
    c: Horizontal(g6)
    c: DistanceX(g6,g6) = 5.5
FEATURE [Part::Revolution] Revolve
  Angle = -30
  Axis = (1,0,0)
  Base = (10,-55,7)
  Solid = true
  Source = -> Sketch022
FEATURE [Part::Cut] Cut
  Base = -> Pocket007
  Tool = -> Revolve
FEATURE [PartDesign::Fillet] Fillet007
  Base = -> Cut [Edge240,Edge279]
  Radius = 2.5
FEATURE [PartDesign::Fillet] Fillet008
  Base = -> Fillet007 [Edge16,Edge11]
  Radius = 3.5
FEATURE [PartDesign::Fillet] Fillet009
  Base = -> Fillet008 [Edge66,Edge184]
  Radius = 3
FEATURE [Sketcher::SketchObject] Sketch023
  Placement = pos=(-25,0,0) rot=(0.57735,-0.57735,-0.57735;2.0944rad)
  Support = -> Fillet009 [Face115]
  sketch-geometry (4):
    g0: ArcOfCircle CenterX=-5 CenterY=9 CenterZ=0 NormalX=0 NormalY=0 NormalZ=1 Radius=1.5 StartAngle=1.5708 EndAngle=4.71239
    g1: ArcOfCircle CenterX=10 CenterY=9 CenterZ=0 NormalX=0 NormalY=0 NormalZ=1 Radius=1.5 StartAngle=4.71239 EndAngle=7.85398
    g2: LineSegment StartX=-5 StartY=7.5 StartZ=0 EndX=10 EndY=7.5 EndZ=0
    g3: LineSegment StartX=-5 StartY=10.5 StartZ=0 EndX=10 EndY=10.5 EndZ=0
  constraints (10):
    c: Tangent(g0,g3) = 1.5708
    c: Tangent(g0,g2) = -1.5708
    c: Tangent(g2,g1) = -1.5708
    c: Tangent(g3,g1) = 1.5708
    c: Horizontal(g2)
    c: Equal(g0,g1)
    c: Distance(g3) = 15
    c: Radius(g1) = 1.5
    c: DistanceX(g0,g-1) = 5
    c: DistanceY(g-1,g0) = 9
FEATURE [PartDesign::Pocket] Pocket008
  Length = 5
  Sketch = -> Sketch023
  Type = 0
FEATURE [PartDesign::Fillet] Fillet010
  Base = -> Pocket008 [Edge350,Edge349,Edge348,Edge347]
  Radius = 1
FEATURE [PartDesign::Fillet] Fillet011
  Base = -> Fillet010 [Edge636,Edge621,Edge622,Edge623,Edge638,Edge637]
  Radius = 0.5
FEATURE [PartDesign::Fillet] Fillet012
  Base = -> Fillet011 [Edge87,Edge92,Edge94,Edge96,Edge98,Edge100,Edge93,Edge77,Edge32,Edge89]
  Radius = 1
FEATURE [PartDesign::Fillet] Fillet013
  Base = -> Fillet012 [Edge282,Edge129,Edge127,Edge125,Edge124,Edge38,Edge37,Edge36,Edge34,Edge32,Edge107,Edge84,Edge110,Edge112,Edge256]
  Radius = 0.5
FEATURE [Part::Cylinder] Cylinder
  Angle = 360
  Height = 5
  Placement = pos=(22,-40,27) rot=(0,1,0;0.785398rad)
  Radius = 3
FEATURE [Part::Mirroring] Part__Mirroring001  label="Cylinder (Mirror #2)"
  Base = (0,0,0)
  Normal = (1,0,0)
  Source = -> Cylinder
FEATURE [Part::MultiFuse] Fusion001
  Shapes = -> [Cylinder,Part__Mirroring001,Fillet013]
FEATURE [Sketcher::SketchObject] Sketch024
  Placement = pos=(28.0355,0,28.0355) rot=(0.357407,0.357407,0.862856;1.71777rad)
  Support = -> Fusion001 [Face1]
  sketch-geometry (1):
    g0: Circle CenterX=-40 CenterY=3.5 CenterZ=0 NormalX=0 NormalY=0 NormalZ=1 Radius=1
  constraints (3):
    c: Radius(g0) = 1
    c: DistanceX(g0,g-1) = 40
    c: DistanceY(g-1,g0) = 3.5
FEATURE [PartDesign::Pocket] Pocket009
  Length = 10
  Sketch = -> Sketch024
  Type = 0
FEATURE [Sketcher::SketchObject] Sketch025
  Placement = pos=(-28.0355,0,28.0355) rot=(0.357407,-0.357407,-0.862856;1.71777rad)
  Support = -> Pocket009 [Face101]
  sketch-geometry (1):
    g0: Circle CenterX=40 CenterY=3.5 CenterZ=0 NormalX=0 NormalY=0 NormalZ=1 Radius=1
  constraints (3):
    c: Radius(g0) = 1
    c: DistanceY(g-1,g0) = 3.5
    c: DistanceX(g-1,g0) = 40
FEATURE [PartDesign::Pocket] Pocket010
  Length = 10
  Sketch = -> Sketch025
  Type = 0
FEATURE [PartDesign::Fillet] Fillet014
  Base = -> Pocket010 [Edge1,Edge161]
  Radius = 1
FEATURE [PartDesign::Fillet] Fillet015
  Base = -> Fillet014 [Edge395,Edge397,Edge252,Edge255]
  Radius = 1
FEATURE [Sketcher::SketchObject] Sketch026
  Placement = pos=(0,55,0) rot=(0,0.707107,0.707107;3.14159rad)
  Support = -> Fillet015 [Face78]
  sketch-geometry (4):
    g0: LineSegment StartX=-5 StartY=29.5 StartZ=0 EndX=15 EndY=29.5 EndZ=0
    g1: LineSegment StartX=15 StartY=29.5 StartZ=0 EndX=15 EndY=8.5 EndZ=0
    g2: LineSegment StartX=15 StartY=8.5 StartZ=0 EndX=-5 EndY=8.5 EndZ=0
    g3: LineSegment StartX=-5 StartY=8.5 StartZ=0 EndX=-5 EndY=29.5 EndZ=0
  constraints (12):
    c: Coincident(g0,g1)
    c: Coincident(g1,g2)
    c: Coincident(g2,g3)
    c: Coincident(g3,g0)
    c: Horizontal(g0)
    c: Horizontal(g2)
    c: Vertical(g1)
    c: Vertical(g3)
    c: Distance(g2) = 20
    c: Distance(g3) = 21
    c: DistanceY(g-1,g2) = 8.5
    c: DistanceX(g2,g-1) = 5
FEATURE [PartDesign::Pocket] Pocket011
  Length = 5
  Sketch = -> Sketch026
  Type = 0
FEATURE [Sketcher::SketchObject] Sketch027
  ExternalGeometry = -> [Pocket011]
  Placement = pos=(0,53.5,0) rot=(1,0,0;1.5708rad)
  Support = -> Pocket011 [Face128]
  sketch-geometry (8):
    g0: LineSegment StartX=5 StartY=29.5 StartZ=0 EndX=-15 EndY=29.5 EndZ=0
    g1: LineSegment StartX=-15 StartY=29.5 StartZ=0 EndX=-15 EndY=8.5 EndZ=0
    g2: LineSegment StartX=-15 StartY=8.5 StartZ=0 EndX=5 EndY=8.5 EndZ=0
    g3: LineSegment StartX=5 StartY=8.5 StartZ=0 EndX=5 EndY=29.5 EndZ=0
    g4: LineSegment StartX=6.5 StartY=31 StartZ=0 EndX=-16.5 EndY=31 EndZ=0
    g5: LineSegment StartX=-16.5 StartY=31 StartZ=0 EndX=-16.5 EndY=7 EndZ=0
    g6: LineSegment StartX=-16.5 StartY=7 StartZ=0 EndX=6.5 EndY=7 EndZ=0
    g7: LineSegment StartX=6.5 StartY=7 StartZ=0 EndX=6.5 EndY=31 EndZ=0
  constraints (22):
    c: Coincident(g0,g1)
    c: Coincident(g1,g2)
    c: Coincident(g2,g3)
    c: Coincident(g3,g0)
    c: Horizontal(g0)
    c: Horizontal(g2)
    c: Vertical(g1)
    c: Vertical(g3)
    c: Coincident(g0,g-5)
    c: Coincident(g1,g-6)
    c: Coincident(g4,g5)
    c: Coincident(g5,g6)
    c: Coincident(g6,g7)
    c: Coincident(g7,g4)
    c: Horizontal(g4)
    c: Horizontal(g6)
    c: Vertical(g5)
    c: Vertical(g7)
    c: DistanceX(g5,g1) = 1.5
    c: DistanceY(g5,g1) = 1.5
    c: DistanceY(g0,g4) = 1.5
    c: DistanceX(g0,g4) = 1.5
FEATURE [PartDesign::Pad] Pad010
  Length = 4.5
  Length2 = 100
  Sketch = -> Sketch027
  Type = 0
FEATURE [PartDesign::Fillet] Fillet016
  Base = -> Pad010 [Edge150,Edge149,Edge148,Edge268,Edge270,Edge440,Edge442,Edge278,Edge279]
  Radius = 0.4
FEATURE [Sketcher::SketchObject] Sketch028
  Placement = pos=(0,0,5) rot=(0,0,1;0rad)
  Support = -> Fillet016 [Face402]
  sketch-geometry (4):
    g0: LineSegment StartX=-16 StartY=42.5 StartZ=0 EndX=6 EndY=42.5 EndZ=0
    g1: LineSegment StartX=6 StartY=42.5 StartZ=0 EndX=6 EndY=40.5 EndZ=0
    g2: LineSegment StartX=6 StartY=40.5 StartZ=0 EndX=-16 EndY=40.5 EndZ=0
    g3: LineSegment StartX=-16 StartY=40.5 StartZ=0 EndX=-16 EndY=42.5 EndZ=0
  constraints (12):
    c: Coincident(g0,g1)
    c: Coincident(g1,g2)
    c: Coincident(g2,g3)
    c: Coincident(g3,g0)
    c: Horizontal(g0)
    c: Horizontal(g2)
    c: Vertical(g1)
    c: Vertical(g3)
    c: Distance(g3) = 2
    c: Distance(g0) = 22
    c: DistanceY(g-1,g1) = 40.5
    c: DistanceX(g2,g-1) = 16
FEATURE [PartDesign::Pad] Pad011
  Length = 5
  Length2 = 100
  Sketch = -> Sketch028
  Type = 0
